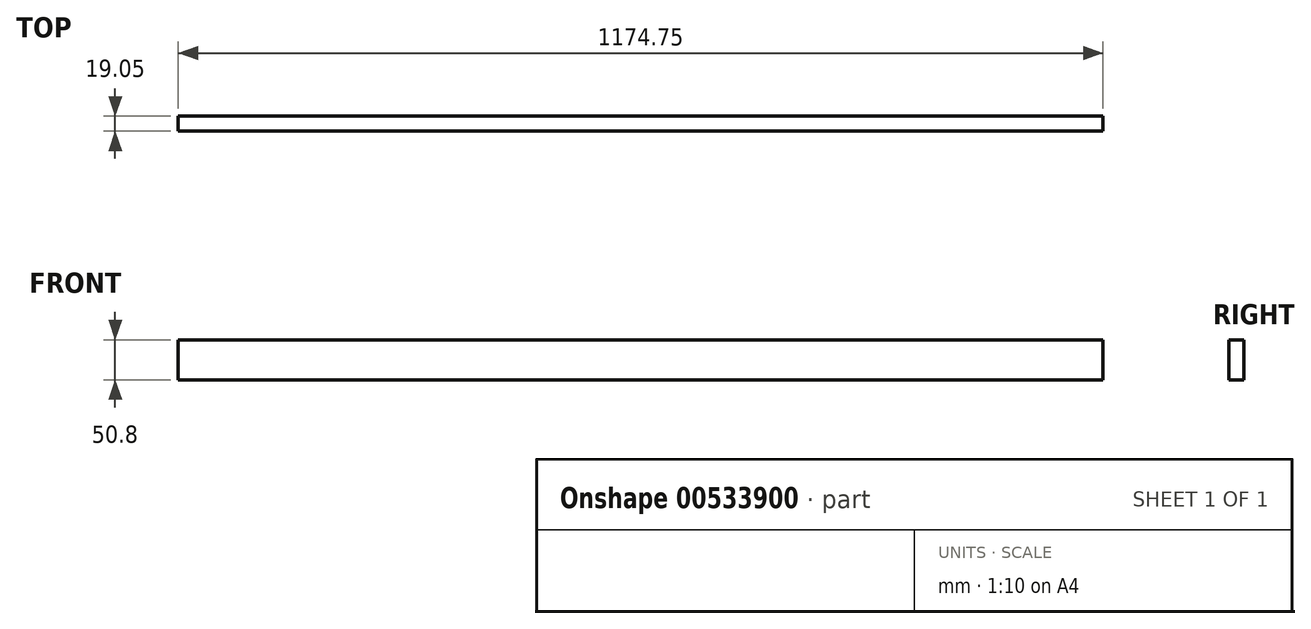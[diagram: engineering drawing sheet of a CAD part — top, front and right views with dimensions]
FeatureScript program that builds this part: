
annotation { "Feature Type Name" : "Feature", "Feature Type Description" : "" }
export const myFeature = defineFeature(function(context is Context, id is Id, definition is map)
    precondition{}
    {
        {
            var Q0;
            Q0=qCreatedBy(makeId("Front.planeOp"),FACE);
            var sketch = newSketch(context, id + "F0", { "sketchPlane" : qUnion([Q0])});
            skLineSegment(sketch, "E0", {"start": v(28.98, 58.59) * mm, "end": v(28.98, 7.79) * mm});
            skLineSegment(sketch, "E1", {"start": v(28.98, 7.79) * mm, "end": v(1203.73, 7.79) * mm});
            skLineSegment(sketch, "E2", {"start": v(1203.73, 7.79) * mm, "end": v(1203.73, 58.59) * mm});
            skLineSegment(sketch, "E3", {"start": v(28.98, 58.59) * mm, "end": v(1203.73, 58.59) * mm});
            skPoint(sketch, "E3.endSnap0", {"position": v(1203.73, 58.59) * mm});
            skPoint(sketch, "E4.orphan", {"position": v(1203.73, 109.39) * mm});
            skPoint(sketch, "E5.orphan", {"position": v(1077.84, 58.59) * mm});
            skSolve(sketch);
        }
        {
            var Q0;
            Q0 = qSketchRegion(id + "F0", true);
            extrude(context, id + "F1", {"entities" : qUnion([Q0]), "depth" : 19.05 * mm, "offsetDistance" : 25.4 * mm});
        }
    });
